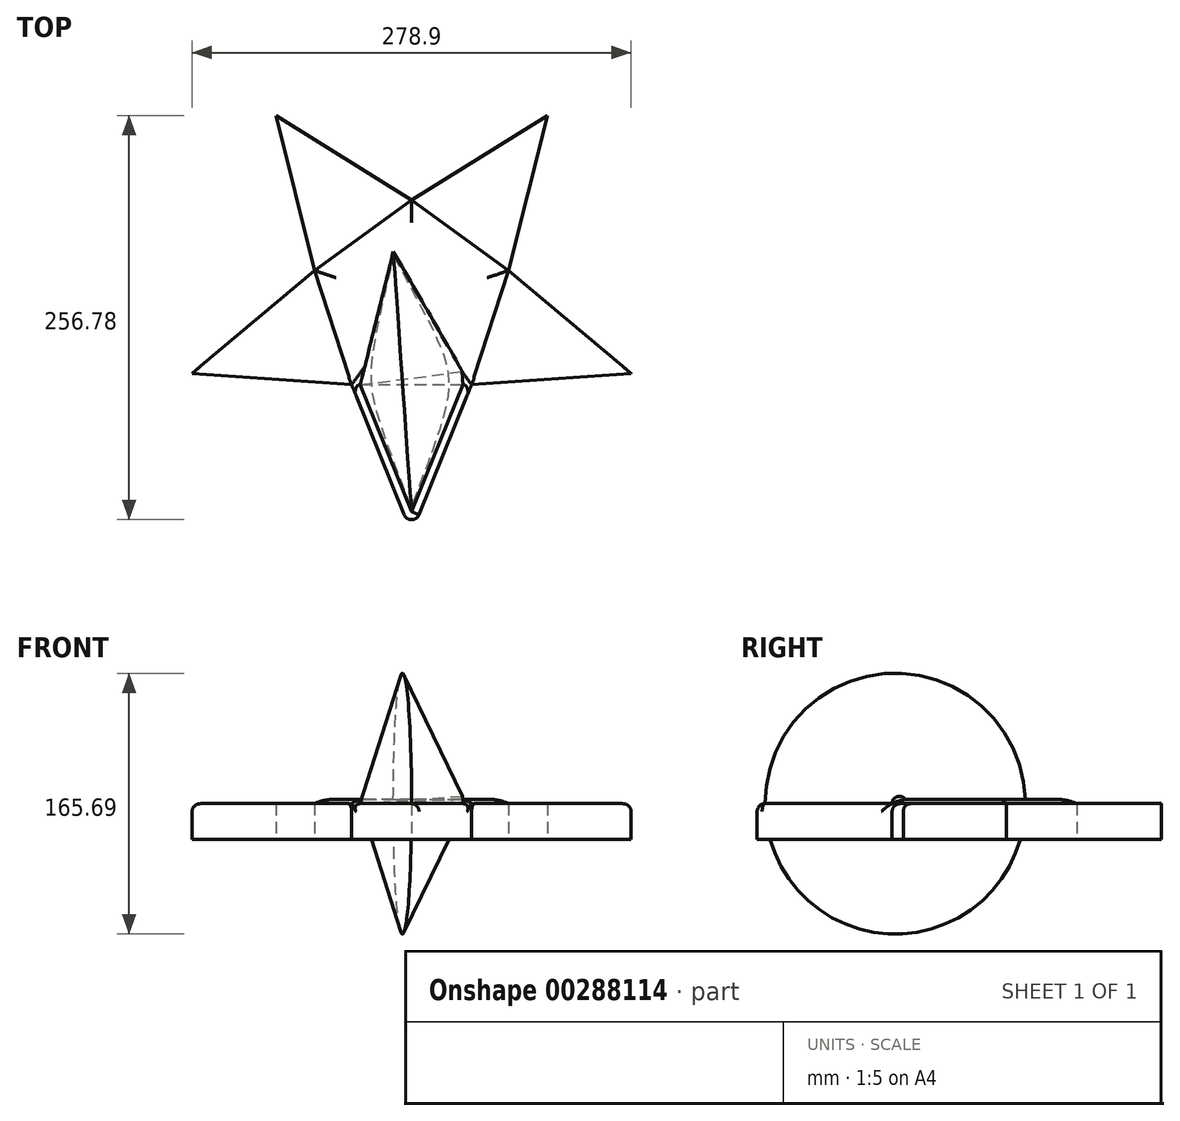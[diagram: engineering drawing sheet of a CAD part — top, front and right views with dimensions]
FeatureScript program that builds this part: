
annotation { "Feature Type Name" : "Feature", "Feature Type Description" : "" }
export const myFeature = defineFeature(function(context is Context, id is Id, definition is map)
    precondition{}
    {
        {
            var Q0;
            Q0=qCreatedBy(makeId("Top.planeOp"),FACE);
            var sketch = newSketch(context, id + "F0", { "sketchPlane" : qUnion([Q0])});
            skCircle(sketch, "E0.cCircle", {"center": v(0, 0) * mm, "radius": 52.44 * mm, "construction": true});
            skLineSegment(sketch, "E0.0", {"start": v(0, 64.82) * mm, "end": v(61.65, 20.03) * mm});
            skLineSegment(sketch, "E0.1", {"start": v(61.65, 20.03) * mm, "end": v(38.1, -52.44) * mm});
            skLineSegment(sketch, "E0.2", {"start": v(38.1, -52.44) * mm, "end": v(-38.1, -52.44) * mm});
            skLineSegment(sketch, "E0.3", {"start": v(-38.1, -52.44) * mm, "end": v(-61.65, 20.03) * mm});
            skLineSegment(sketch, "E0.4", {"start": v(-61.65, 20.03) * mm, "end": v(0, 64.82) * mm});
            skLineSegment(sketch, "E1", {"start": v(-86.18, 118.62) * mm, "end": v(0, 64.82) * mm});
            skLineSegment(sketch, "E2", {"start": v(0, 64.82) * mm, "end": v(86.18, 118.62) * mm});
            skLineSegment(sketch, "E3", {"start": v(86.18, 118.62) * mm, "end": v(61.65, 20.03) * mm});
            skLineSegment(sketch, "E4", {"start": v(61.65, 20.03) * mm, "end": v(139.45, -45.3) * mm});
            skLineSegment(sketch, "E5", {"start": v(139.45, -45.3) * mm, "end": v(38.1, -52.44) * mm});
            skLineSegment(sketch, "E6", {"start": v(38.1, -52.44) * mm, "end": v(0, -146.63) * mm});
            skLineSegment(sketch, "E7", {"start": v(0, -146.63) * mm, "end": v(-38.1, -52.44) * mm});
            skLineSegment(sketch, "E8", {"start": v(-38.1, -52.44) * mm, "end": v(-139.45, -45.3) * mm});
            skLineSegment(sketch, "E9", {"start": v(-139.45, -45.3) * mm, "end": v(-61.65, 20.03) * mm});
            skLineSegment(sketch, "E10", {"start": v(139.45, -45.3) * mm, "end": v(195.35, -63.47) * mm});
            skPoint(sketch, "E11.start.orphan", {"position": v(0, -52.44) * mm});
            skPoint(sketch, "E12.orphan", {"position": v(49.87, -16.2) * mm});
            skLineSegment(sketch, "E13", {"start": v(-61.65, 20.03) * mm, "end": v(-86.18, 118.62) * mm});
            skSolve(sketch);
        }
        {
            var Q0;
            Q0=makeQuery(id+"F0.imprint","IMPRINT",FACE,{"disambiguationData":[TD([[makeQuery(id+"F0.imprint","IMPRINT",EDGE,{"derivedFrom":sQuery(id+"F0.wireOp",EDGE,"E0.3")}),1.0]])]});
            var Q1;
            Q1=makeQuery(id+"F0.imprint","IMPRINT",FACE,{"disambiguationData":[TD([[makeQuery(id+"F0.imprint","IMPRINT",EDGE,{"derivedFrom":sQuery(id+"F0.wireOp",EDGE,"E0.4")}),1.0]])]});
            var Q2;
            Q2=makeQuery(id+"F0.imprint","IMPRINT",FACE,{"disambiguationData":[TD([[makeQuery(id+"F0.imprint","IMPRINT",EDGE,{"derivedFrom":sQuery(id+"F0.wireOp",EDGE,"E0.0")}),1.0]])]});
            var Q3;
            Q3=makeQuery(id+"F0.imprint","IMPRINT",FACE,{"disambiguationData":[TD([[makeQuery(id+"F0.imprint","IMPRINT",EDGE,{"derivedFrom":sQuery(id+"F0.wireOp",EDGE,"E0.1")}),1.0]])]});
            var Q4;
            Q4=makeQuery(id+"F0.imprint","IMPRINT",FACE,{"disambiguationData":[TD([[makeQuery(id+"F0.imprint","IMPRINT",EDGE,{"derivedFrom":sQuery(id+"F0.wireOp",EDGE,"E0.0")}),-1.0]])]});
            var Q5;
            Q5=makeQuery(id+"F0.imprint","IMPRINT",FACE,{"disambiguationData":[TD([[makeQuery(id+"F0.imprint","IMPRINT",EDGE,{"derivedFrom":sQuery(id+"F0.wireOp",EDGE,"E0.2")}),1.0]])]});
            extrude(context, id + "F1", {"entities" : qUnion([Q0, Q1, Q2, Q3, Q4, Q5]), "depth" : 22.58 * mm});
        }
        {
            var Q0;
            Q0=makeQuery(id+"F0.imprint","IMPRINT",FACE,{"disambiguationData":[TD([[makeQuery(id+"F0.imprint","IMPRINT",EDGE,{"derivedFrom":sQuery(id+"F0.wireOp",EDGE,"E0.0")}),-1.0]])]});
            extrude(context, id + "F2", {"entities" : qUnion([Q0]), "operationType" : NewBodyOperationType.ADD, "depth" : 25.4 * mm});
        }
        {
            var Q0;
            Q0=makeQuery(id+"F2.opExtrude","CAP_EDGE",EDGE,{"disambiguationData":[OSD([sQuery(id+"F0.wireOp",EDGE,"E0.0")])],"isStart":false});
            fillet(context, id + "F3", {"entities" : qUnion([Q0]), "radius" : 25.4 * mm, "tangentPropagation" : true, "allowEdgeOverflow" : false});
        }
        {
            var Q0;
            Q0=makeQuery(id+"F2.opExtrude","CAP_EDGE",EDGE,{"disambiguationData":[OSD([sQuery(id+"F0.wireOp",EDGE,"E0.1")])],"isStart":false});
            var Q1;
            Q1=makeQuery(id+"F2.opExtrude","CAP_EDGE",EDGE,{"disambiguationData":[OSD([sQuery(id+"F0.wireOp",EDGE,"E0.2")])],"isStart":false});
            var Q2;
            Q2=makeQuery(id+"F2.opExtrude","CAP_EDGE",EDGE,{"disambiguationData":[OSD([sQuery(id+"F0.wireOp",EDGE,"E0.4")])],"isStart":false});
            var Q3;
            Q3=makeQuery(id+"F2.opExtrude","CAP_EDGE",EDGE,{"disambiguationData":[OSD([sQuery(id+"F0.wireOp",EDGE,"E0.3")])],"isStart":false});
            fillet(context, id + "F4", {"entities" : qUnion([Q0, Q1, Q2, Q3]), "radius" : 25.4 * mm, "tangentPropagation" : true, "allowEdgeOverflow" : false});
        }
        {
            var Q0;
            Q0=makeQuery(id+"F1.opExtrude","CAP_EDGE",EDGE,{"disambiguationData":[OSD([sQuery(id+"F0.wireOp",EDGE,"E5")])],"isStart":false});
            fillet(context, id + "F5", {"entities" : qUnion([Q0]), "radius" : 5.08 * mm, "tangentPropagation" : true, "allowEdgeOverflow" : false});
        }
        {
            var Q0;
            Q0=makeQuery(id+"F1.opExtrude","CAP_EDGE",EDGE,{"disambiguationData":[OSD([sQuery(id+"F0.wireOp",EDGE,"E6")])],"isStart":false});
            fillet(context, id + "F6", {"entities" : qUnion([Q0]), "radius" : 5.08 * mm, "tangentPropagation" : true, "allowEdgeOverflow" : false});
        }
        {
            var Q0;
            Q0=makeQuery(id+"F1.opExtrude","CAP_EDGE",EDGE,{"disambiguationData":[OSD([sQuery(id+"F0.wireOp",EDGE,"E8")])],"isStart":false});
            fillet(context, id + "F7", {"entities" : qUnion([Q0]), "radius" : 5.08 * mm, "tangentPropagation" : true, "allowEdgeOverflow" : false});
        }
        {
            var Q0;
            Q0=makeQuery(id+"F1.opExtrude","CAP_EDGE",EDGE,{"disambiguationData":[OSD([sQuery(id+"F0.wireOp",EDGE,"E7")])],"isStart":false});
            fillet(context, id + "F8", {"entities" : qUnion([Q0]), "radius" : 5.08 * mm, "tangentPropagation" : true, "allowEdgeOverflow" : false});
        }
        {
            var Q0;
            {var subQ0=sQuery(id+"F0.wireOp",EDGE,"E7");var subQ1=sQuery(id+"F0.wireOp",EDGE,"E5");var subQ2=sQuery(id+"F0.wireOp",EDGE,"E6");var subQ3=sQuery(id+"F0.wireOp",EDGE,"E8");var subQ4=makeQuery(id+"F1.opExtrude","CAP_FACE",FACE,{"disambiguationData":[OSD([sQuery(id+"F0.wireOp",EDGE,"E1"),sQuery(id+"F0.wireOp",EDGE,"E2"),sQuery(id+"F0.wireOp",EDGE,"E3"),sQuery(id+"F0.wireOp",EDGE,"E4"),subQ1,subQ2,subQ0,subQ3,sQuery(id+"F0.wireOp",EDGE,"E9"),sQuery(id+"F0.wireOp",EDGE,"E13")])],"isStart":false});Q0=makeQuery(id+"F2.boolean.opBoolean","SPLIT",FACE,{"disambiguationData":[TD([subQ4,makeQuery(id+"F1.opExtrude","SWEPT_FACE",FACE,{"disambiguationData":[OSD([subQ1])]}),makeQuery(id+"F1.opExtrude","SWEPT_FACE",FACE,{"disambiguationData":[OSD([subQ2])]}),makeQuery(id+"F1.opExtrude","SWEPT_FACE",FACE,{"disambiguationData":[OSD([subQ0])]}),makeQuery(id+"F1.opExtrude","SWEPT_FACE",FACE,{"disambiguationData":[OSD([subQ3])]}),makeQuery(id+"F2.opExtrude","SWEPT_FACE",FACE,{"disambiguationData":[OSD([sQuery(id+"F0.wireOp",EDGE,"E0.1")])]}),makeQuery(id+"F2.opExtrude","SWEPT_FACE",FACE,{"disambiguationData":[OSD([sQuery(id+"F0.wireOp",EDGE,"E0.2")])]}),makeQuery(id+"F2.opExtrude","SWEPT_FACE",FACE,{"disambiguationData":[OSD([sQuery(id+"F0.wireOp",EDGE,"E0.3")])]})])],"derivedFrom":subQ4});}
            var Q1;
            {var subQ0=sQuery(id+"F0.wireOp",EDGE,"E5");var subQ1=sQuery(id+"F0.wireOp",EDGE,"E4");var subQ2=sQuery(id+"F0.wireOp",EDGE,"E3");var subQ3=sQuery(id+"F0.wireOp",EDGE,"E6");var subQ4=makeQuery(id+"F1.opExtrude","CAP_FACE",FACE,{"disambiguationData":[OSD([sQuery(id+"F0.wireOp",EDGE,"E1"),sQuery(id+"F0.wireOp",EDGE,"E2"),subQ2,subQ1,subQ0,subQ3,sQuery(id+"F0.wireOp",EDGE,"E7"),sQuery(id+"F0.wireOp",EDGE,"E8"),sQuery(id+"F0.wireOp",EDGE,"E9"),sQuery(id+"F0.wireOp",EDGE,"E13")])],"isStart":false});Q1=makeQuery(id+"F5.opFillet","BLEND_EDGE",EDGE,{"blendedFrom":[makeQuery(id+"F1.opExtrude","CAP_EDGE",EDGE,{"disambiguationData":[OSD([subQ0])],"isStart":false}),makeQuery(id+"F2.boolean.opBoolean","SPLIT",FACE,{"disambiguationData":[TD([subQ4,makeQuery(id+"F1.opExtrude","SWEPT_FACE",FACE,{"disambiguationData":[OSD([subQ2])]}),makeQuery(id+"F1.opExtrude","SWEPT_FACE",FACE,{"disambiguationData":[OSD([subQ1])]}),makeQuery(id+"F1.opExtrude","SWEPT_FACE",FACE,{"disambiguationData":[OSD([subQ0])]}),makeQuery(id+"F1.opExtrude","SWEPT_FACE",FACE,{"disambiguationData":[OSD([subQ3])]}),makeQuery(id+"F2.opExtrude","SWEPT_FACE",FACE,{"disambiguationData":[OSD([sQuery(id+"F0.wireOp",EDGE,"E0.0")])]}),makeQuery(id+"F2.opExtrude","SWEPT_FACE",FACE,{"disambiguationData":[OSD([sQuery(id+"F0.wireOp",EDGE,"E0.1")])]}),makeQuery(id+"F2.opExtrude","SWEPT_FACE",FACE,{"disambiguationData":[OSD([sQuery(id+"F0.wireOp",EDGE,"E0.2")])]})])],"derivedFrom":subQ4})],"blendedInto":[makeQuery(id+"F2.boolean.opBoolean","SPLIT",FACE,{"disambiguationData":[TD([subQ4,makeQuery(id+"F1.opExtrude","SWEPT_FACE",FACE,{"disambiguationData":[OSD([subQ2])]}),makeQuery(id+"F1.opExtrude","SWEPT_FACE",FACE,{"disambiguationData":[OSD([subQ1])]}),makeQuery(id+"F1.opExtrude","SWEPT_FACE",FACE,{"disambiguationData":[OSD([subQ0])]}),makeQuery(id+"F1.opExtrude","SWEPT_FACE",FACE,{"disambiguationData":[OSD([subQ3])]}),makeQuery(id+"F2.opExtrude","SWEPT_FACE",FACE,{"disambiguationData":[OSD([sQuery(id+"F0.wireOp",EDGE,"E0.0")])]}),makeQuery(id+"F2.opExtrude","SWEPT_FACE",FACE,{"disambiguationData":[OSD([sQuery(id+"F0.wireOp",EDGE,"E0.1")])]}),makeQuery(id+"F2.opExtrude","SWEPT_FACE",FACE,{"disambiguationData":[OSD([sQuery(id+"F0.wireOp",EDGE,"E0.2")])]})])],"derivedFrom":subQ4})]});}
            revolve(context, id + "F9", {"operationType" : NewBodyOperationType.ADD, "entities" : qUnion([Q0]), "axis" : qUnion([Q1]), "revolveType" : RevolveType.FULL});
        }
    });
